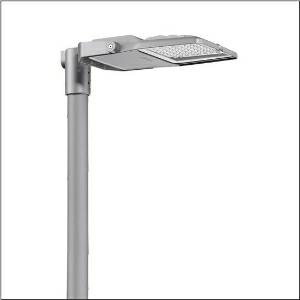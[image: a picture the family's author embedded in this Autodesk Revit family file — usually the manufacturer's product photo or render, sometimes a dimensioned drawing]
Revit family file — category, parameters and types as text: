
# Revit family: floodlight_fl_21_iq_mini___pl52_5xa7771d4d3a_bc98
name_source: partatom
category: Lighting Fixtures
units: mm (PartAtom-declared; Revit-internal decimal feet)

## family parameters
Cut with Voids When Loaded = No
Host = Face
Light Source = No
Part Type = Normal
Room Calculation Point = No
Round Connector Dimension = Use Diameter
Shared = No

## types (1)
- --- (1 x LED, 18610 lm, 143 W, 4000K)
    Apparent Load = 143 VA
    CIE Flux Codes = 26 60 98 100 100
    Color Rendering = 70
    Color Temperature = 4000K
    Default Elevation = 1800 mm
    Description = Floodlight FL 21 iQ mini, floodlight, primary light control with lens, of PMMA, primary optical cover: protective disc, of toughened safety glass, transparent, light distribution: PL52, light emission: direct distribution, installation type: surface-mounted, LED, High Power LED, rated luminous flux: 18.610lm, luminous efficacy: 130lm/W, light colour: 740, colour temperature: 4000K, control gear: iQ Comfort/DALI, control: Auto-Match, Temp-Guard, Lumen-Switch, Night-Set, Smart-Wire, Light-Fading, Desk-Remote (wireless, voltage-free reading and setting of iQ features in the workshop via application-optimized NFC function/RFID function), optimised constant luminous flux control (CLO 2.0), with terminal, 6-pole, mains connection: 220..240V, AC, 50/60Hz, start of lifetime: 143W, end of service life: 152W, reduction: 61W, luminaire housing, of diecast aluminium, powder-coated, Siteco® metallic grey (DB 702S), corrosivity category C5 mid according to DIN EN ISO 12944, suitable for swimming pools, chlorine-resistant, sealing non-destructively replaceable, please order mast flange separately, mast bracket, of steel, galvanised, powder-coated, Siteco® metallic grey (DB 702S), protection rating (complete): IP66, insulation class (complete): insulation class II (safety insulation), certification: CE, ENEC, VDE, protection symbol: D, impact resistance: IK08, permissible operating ambient temperature: -40..+40°C, permissible operating ambient temperature for outdoor applications: -40..+50°C, standard: DIN EN 12944, LABS conformity tested according to VDMA 24364:2018-05, packaging unit: 1 piece

Light Distribution: PL52
    Height = 70 mm
    Lamp = 1 x LED
    Lamp Light Flux = 18610 lm
    Lamp Power = 143 W
    Lamp count = 1
    Length = 485 mm
    Luminous efficacy = 130 lm/W
    Manufacturer = Siteco
    ModVariant = No
    Model = 5XA7771D4D3A
    Number of Poles = 1
    OnlyDefault = Yes
    Power Factor = 1
    Product Name = Floodlight FL 21 iQ mini | PL52
    Product group = floodlight | pylon annexe
    ProductGroupID = 6200
    Protection Class = Protection class II
    Protection Degree = IP 66
    RLX_Detail_Level = 1
    RLX_Emergency_Light_Flux = 0 lm
    RLX_Emergency_Type = 0
    RLX_Emergency_Type_DB = No
    RlxData = <blob elided: 101901 chars, md5=b3c0f954>
    Socket = socket
    Standby Power = 0 W
    System Light Flux = 18610 lm
    System Power = 143 W
    Type Comments = factory setting: luminous flux: 100 % | dim-lin: 254 | 730 mA
    Type Image = l_1007125.jpg
    URL = http://relux.com
    VarID = @adj_163864
    Voltage = 0 V
    Weight = 0.00 kg
    Width = 337 mm

## geometry (parser evidence)
native form markers: Blend x4, Sweep x12
no freeform markers — native parametric forms only
